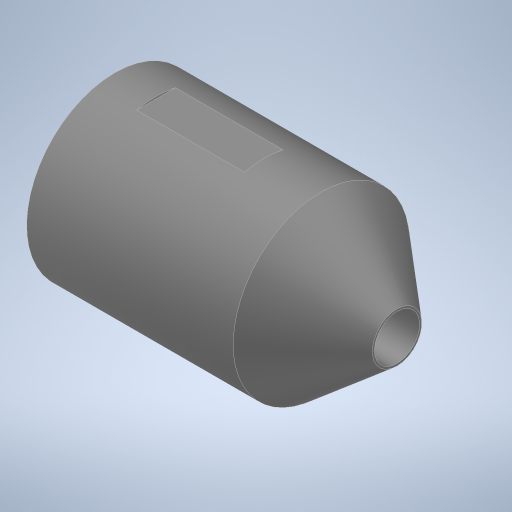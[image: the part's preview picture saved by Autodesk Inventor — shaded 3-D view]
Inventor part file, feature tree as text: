
AUTODESK INVENTOR PART (.ipt)
format: ipt  version: 2023.1 (Build 271208000, 208)  size: 258,048 bytes
history: native  units: in
note: dims shown in document units (in); Inventor stores cm internally (conversion verified against a paired STEP export)
features: imported_body x1, thread x1
ambient origin geometry x8: Origin, YZ Plane, XZ Plane, XY Plane, X Axis, Y Axis, Z Axis, Center Point
bodies: Solid1 (feature_tree)
feature tree (2):
  imported_body  "Base1"
  thread  "Thread1"  [1 undecoded]
note: 1 required parameter value undecoded (feature->parameter linkage not recoverable at this tier; creation-order binding heuristic only, values carry confidence <= 0.55)
